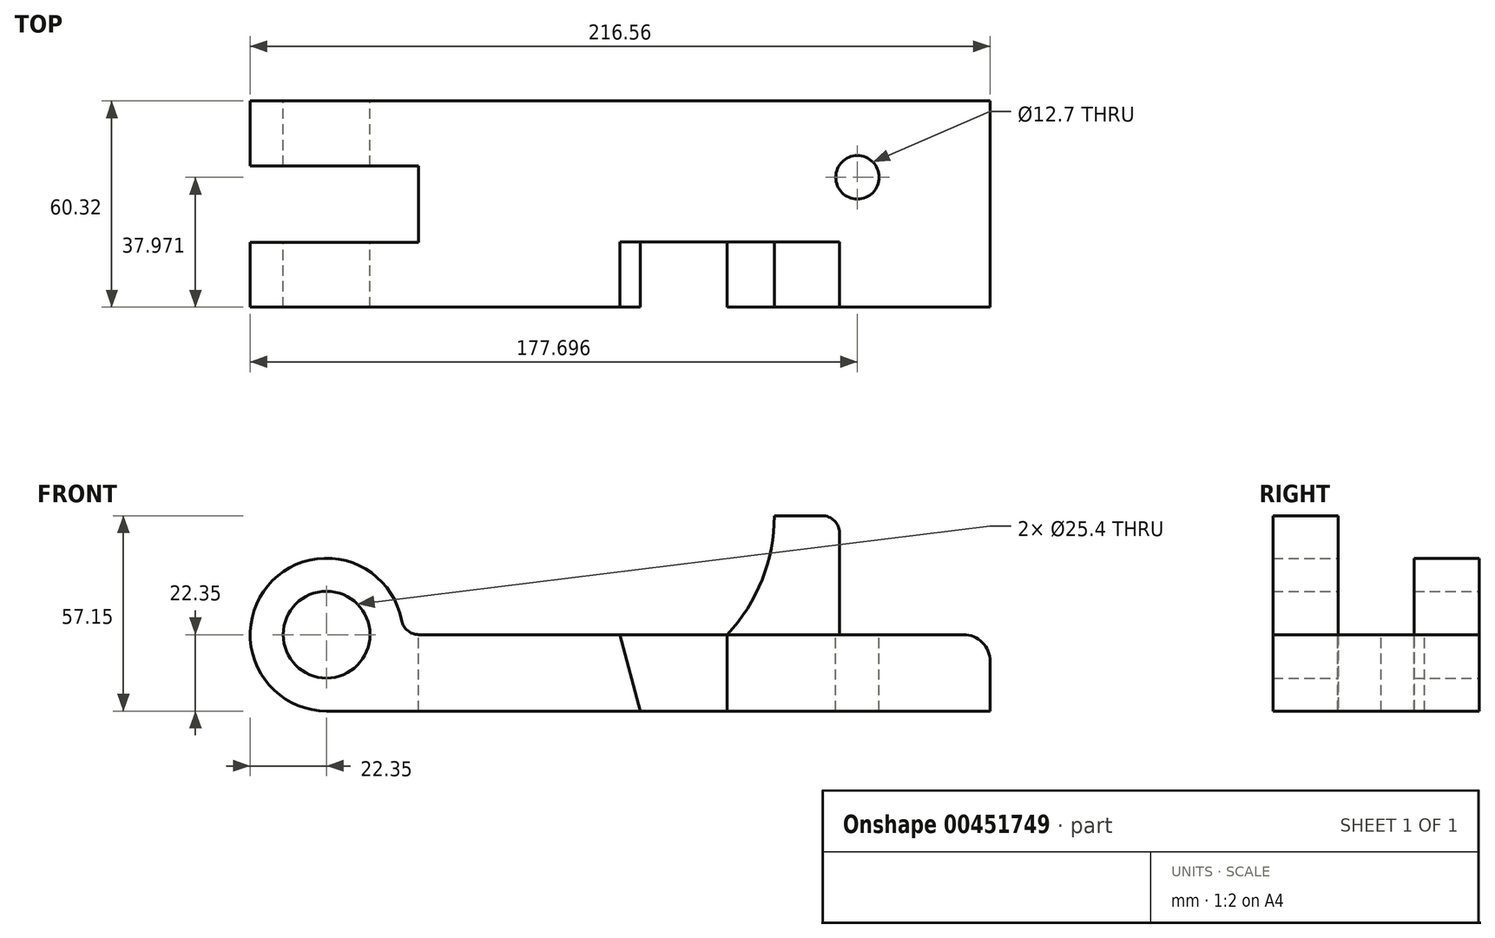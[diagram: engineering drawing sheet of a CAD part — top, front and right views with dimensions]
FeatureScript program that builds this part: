
annotation { "Feature Type Name" : "Feature", "Feature Type Description" : "" }
export const myFeature = defineFeature(function(context is Context, id is Id, definition is map)
    precondition{}
    {
        {
            var Q0;
            Q0=qCreatedBy(makeId("Front.planeOp"),FACE);
            var sketch = newSketch(context, id + "F0", { "sketchPlane" : qUnion([Q0])});
            skCircle(sketch, "E0", {"center": v(0, 0) * mm, "radius": 12.7 * mm});
            skArc(sketch, "E1", {"start": v(21.97, 4.14) * mm, "mid": v(-17.2, 14.27) * mm, "end": v(0, -22.35) * mm});
            skLineSegment(sketch, "E2", {"start": v(0, -22.35) * mm, "end": v(194.2, -22.35) * mm});
            skLineSegment(sketch, "E3", {"start": v(194.2, -22.35) * mm, "end": v(194.2, -7.87) * mm});
            skLineSegment(sketch, "E4", {"start": v(186.33, 0) * mm, "end": v(26.96, 0) * mm});
            skPoint(sketch, "E5.visualSharp", {"position": v(194.2, 0) * mm});
            skArc(sketch, "E5.filletArc", {"start": v(194.2, -7.87) * mm, "mid": v(191.9, -2.3) * mm, "end": v(186.33, 0) * mm});
            skPoint(sketch, "E6.visualSharp", {"position": v(22.35, 0) * mm});
            skArc(sketch, "E6.filletArc", {"start": v(21.97, 4.14) * mm, "mid": v(23.72, 1.17) * mm, "end": v(26.96, 0) * mm});
            skLineSegment(sketch, "E7", {"start": v(26.96, 0) * mm, "end": v(26.96, -22.35) * mm});
            skSolve(sketch);
        }
        {
            var Q0;
            Q0 = qSketchRegion(id + "F0", true);
            extrude(context, id + "F1", {"entities" : qUnion([Q0]), "endBound" : BoundingType.SYMMETRIC, "depth" : 60.32 * mm});
        }
        {
            var Q0;
            Q0=qCreatedBy(makeId("Front.planeOp"),FACE);
            var sketch = newSketch(context, id + "F2", { "sketchPlane" : qUnion([Q0])});
            skCircle(sketch, "E8", {"center": v(0, 0) * mm, "radius": 12.7 * mm});
            skArc(sketch, "E9", {"start": v(21.97, 4.14) * mm, "mid": v(-17.2, 14.27) * mm, "end": v(0, -22.35) * mm});
            skLineSegment(sketch, "E10", {"start": v(0, -22.35) * mm, "end": v(26.96, -22.35) * mm});
            skLineSegment(sketch, "E11", {"start": v(26.96, -22.35) * mm, "end": v(26.96, 0) * mm});
            skLineSegment(sketch, "E12", {"start": v(26.96, 0) * mm, "end": v(26.96, 0) * mm});
            skPoint(sketch, "E13.visualSharp", {"position": v(22.35, 0) * mm});
            skArc(sketch, "E13.filletArc", {"start": v(21.97, 4.14) * mm, "mid": v(23.72, 1.17) * mm, "end": v(26.96, 0) * mm});
            skSolve(sketch);
        }
        {
            var Q0;
            Q0 = qSketchRegion(id + "F2", true);
            extrude(context, id + "F3", {"entities" : qUnion([Q0]), "operationType" : NewBodyOperationType.REMOVE, "endBound" : BoundingType.SYMMETRIC, "oppositeDirection" : true, "depth" : 22.33 * mm});
        }
        {
            var Q0;
            Q0=makeQuery(id+"F1.opExtrude","CAP_FACE",FACE,{"disambiguationData":[OSD([sQuery(id+"F0.wireOp",EDGE,"E0"),sQuery(id+"F0.wireOp",EDGE,"E1"),sQuery(id+"F0.wireOp",EDGE,"E2"),sQuery(id+"F0.wireOp",EDGE,"E3"),sQuery(id+"F0.wireOp",EDGE,"E4"),sQuery(id+"F0.wireOp",EDGE,"E5.filletArc"),sQuery(id+"F0.wireOp",EDGE,"E6.filletArc")])],"isStart":false});
            var sketch = newSketch(context, id + "F4", { "sketchPlane" : qUnion([Q0])});
            skLineSegment(sketch, "E14", {"start": v(85.85, 0) * mm, "end": v(91.85, -22.35) * mm});
            skLineSegment(sketch, "E15", {"start": v(91.85, -22.35) * mm, "end": v(117.25, -22.35) * mm});
            skLineSegment(sketch, "E16", {"start": v(117.25, -22.35) * mm, "end": v(117.25, 0) * mm});
            skLineSegment(sketch, "E17", {"start": v(117.25, 0) * mm, "end": v(85.85, 0) * mm});
            skSolve(sketch);
        }
        {
            var Q0;
            Q0 = qSketchRegion(id + "F4", true);
            extrude(context, id + "F5", {"entities" : qUnion([Q0]), "operationType" : NewBodyOperationType.REMOVE, "oppositeDirection" : true, "depth" : 19.05 * mm});
        }
        {
            var Q0;
            {var subQ0=sQuery(id+"F0.wireOp",EDGE,"E5.filletArc");var subQ1=sQuery(id+"F0.wireOp",EDGE,"E4");var subQ2=sQuery(id+"F0.wireOp",EDGE,"E3");var subQ3=sQuery(id+"F0.wireOp",EDGE,"E2");Q0=makeQuery(id+"F5.boolean.opBoolean","SPLIT",FACE,{"disambiguationData":[TD([makeQuery(id+"F1.opExtrude","SWEPT_FACE",FACE,{"disambiguationData":[OSD([subQ2])]})])],"derivedFrom":makeQuery(id+"F1.opExtrude","CAP_FACE",FACE,{"disambiguationData":[OSD([sQuery(id+"F0.wireOp",EDGE,"E0"),sQuery(id+"F0.wireOp",EDGE,"E1"),subQ3,subQ2,subQ1,subQ0,sQuery(id+"F0.wireOp",EDGE,"E6.filletArc")])],"isStart":false})});}
            var sketch = newSketch(context, id + "F6", { "sketchPlane" : qUnion([Q0])});
            skLineSegment(sketch, "E18", {"start": v(150.09, 0) * mm, "end": v(150.09, 29.72) * mm});
            skLineSegment(sketch, "E19", {"start": v(145, 34.8) * mm, "end": v(131.04, 34.8) * mm});
            skLineSegment(sketch, "E20", {"start": v(131.04, 34.8) * mm, "end": v(131.04, 34.8) * mm});
            skArc(sketch, "E21", {"start": v(117.25, 0) * mm, "mid": v(127.46, 16.08) * mm, "end": v(131.04, 34.8) * mm});
            skPoint(sketch, "E21.first.point", {"position": v(131.04, 34.8) * mm});
            skPoint(sketch, "E21.second.point", {"position": v(117.25, 0) * mm});
            skPoint(sketch, "E21.third.point", {"position": v(29.92, 41.77) * mm});
            skPoint(sketch, "E22.visualSharp", {"position": v(150.09, 34.8) * mm});
            skArc(sketch, "E22.filletArc", {"start": v(150.09, 29.72) * mm, "mid": v(148.6, 33.31) * mm, "end": v(145, 34.8) * mm});
            skLineSegment(sketch, "E23", {"start": v(117.25, 0) * mm, "end": v(150.09, 0) * mm});
            skSolve(sketch);
        }
        {
            var Q0;
            Q0=makeQuery(id+"F6.imprint","IMPRINT",FACE,{"disambiguationData":[TD([[makeQuery(id+"F6.imprint","IMPRINT",EDGE,{"derivedFrom":sQuery(id+"F6.wireOp",EDGE,"E18")}),1.0]])]});
            var Q1;
            Q1 = qConstructionFilter(qBodyType(qCreatedBy(id + "F6" ,EDGE), BodyType.WIRE), ConstructionObject.NO);
            extrude(context, id + "F7", {"entities" : qUnion([Q0]), "surfaceEntities" : qUnion([Q1]), "oppositeDirection" : true, "depth" : 19.05 * mm});
        }
        {
            var Q0;
            Q0=makeQuery(id+"F1.opExtrude","SWEPT_FACE",FACE,{"disambiguationData":[OSD([sQuery(id+"F0.wireOp",EDGE,"E4")])]});
            var sketch = newSketch(context, id + "F8", { "sketchPlane" : qUnion([Q0])});
            skCircle(sketch, "E24", {"center": v(155.35, 7.81) * mm, "radius": 6.35 * mm});
            skPoint(sketch, "E24.first.point", {"position": v(150.97, 3.2) * mm});
            skPoint(sketch, "E24.second.point", {"position": v(160.52, 11.49) * mm});
            skPoint(sketch, "E24.third.point", {"position": v(158.93, 2.57) * mm});
            skSolve(sketch);
        }
        {
            var Q0;
            Q0=makeQuery(id+"F8.imprint","IMPRINT",FACE,{"disambiguationData":[TD([[makeQuery(id+"F8.imprint","IMPRINT",EDGE,{"derivedFrom":sQuery(id+"F8.wireOp",EDGE,"E24")}),1.0]])]});
            extrude(context, id + "F9", {"entities" : qUnion([Q0]), "operationType" : NewBodyOperationType.REMOVE, "endBound" : BoundingType.THROUGH_ALL, "oppositeDirection" : true, "depth" : 25.4 * mm});
        }
    });
